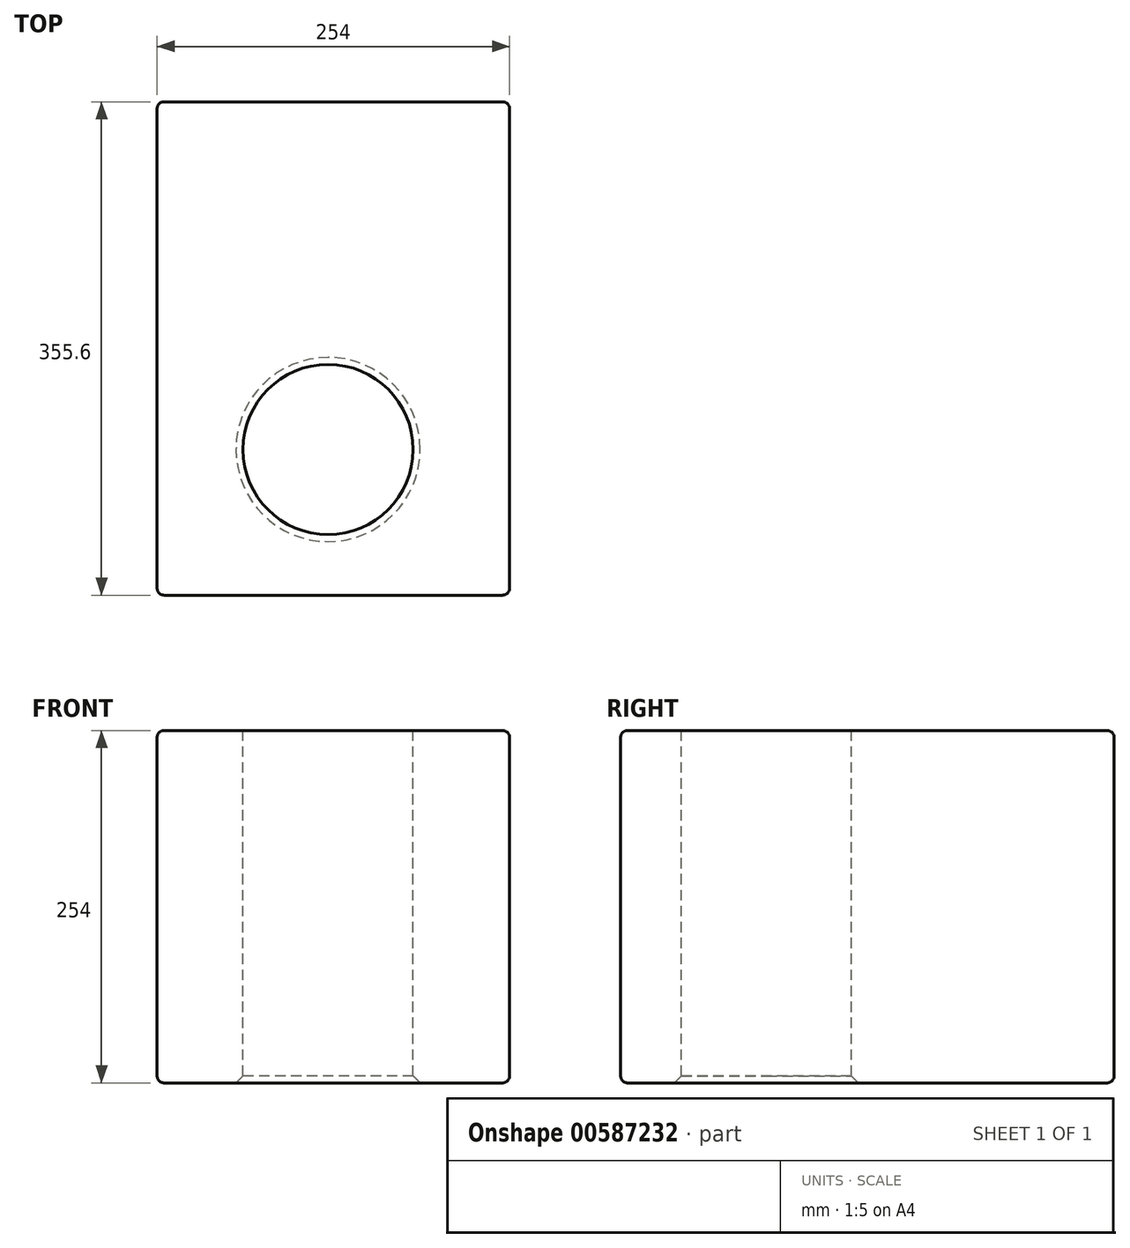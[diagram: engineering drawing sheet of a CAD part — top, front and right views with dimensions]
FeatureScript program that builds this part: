
annotation { "Feature Type Name" : "Feature", "Feature Type Description" : "" }
export const myFeature = defineFeature(function(context is Context, id is Id, definition is map)
    precondition{}
    {
        {
            var Q0;
            Q0=qCreatedBy(makeId("Top.planeOp"),FACE);
            var sketch = newSketch(context, id + "F0", { "sketchPlane" : qUnion([Q0])});
            skLineSegment(sketch, "E0.bottom", {"start": v(0, 0) * mm, "end": v(254, 0) * mm});
            skLineSegment(sketch, "E0.top", {"start": v(0, 355.6) * mm, "end": v(254, 355.6) * mm});
            skLineSegment(sketch, "E0.left", {"start": v(0, 0) * mm, "end": v(0, 355.6) * mm});
            skLineSegment(sketch, "E0.right", {"start": v(254, 0) * mm, "end": v(254, 355.6) * mm});
            skSolve(sketch);
        }
        {
            var Q0;
            Q0=makeQuery(id+"F0.imprint","IMPRINT",FACE,{"disambiguationData":[TD([[makeQuery(id+"F0.imprint","IMPRINT",EDGE,{"derivedFrom":sQuery(id+"F0.wireOp",EDGE,"E0.bottom")}),1.0]])]});
            extrude(context, id + "F1", {"entities" : qUnion([Q0]), "depth" : 254 * mm, "offsetDistance" : 25.4 * mm});
        }
        {
            var Q0;
            Q0=makeQuery(id+"F1.opExtrude","SWEPT_EDGE",EDGE,{"disambiguationData":[OSD([sQuery(id+"F0.wireOp",EDGE,"E0.bottom"),sQuery(id+"F0.wireOp",EDGE,"E0.right")])]});
            var Q1;
            Q1=makeQuery(id+"F1.opExtrude","SWEPT_EDGE",EDGE,{"disambiguationData":[OSD([sQuery(id+"F0.wireOp",EDGE,"E0.top"),sQuery(id+"F0.wireOp",EDGE,"E0.right")])]});
            var Q2;
            Q2=makeQuery(id+"F1.opExtrude","SWEPT_EDGE",EDGE,{"disambiguationData":[OSD([sQuery(id+"F0.wireOp",EDGE,"E0.bottom"),sQuery(id+"F0.wireOp",EDGE,"E0.left")])]});
            var Q3;
            Q3=makeQuery(id+"F1.opExtrude","CAP_EDGE",EDGE,{"disambiguationData":[OSD([sQuery(id+"F0.wireOp",EDGE,"E0.left")])],"isStart":true});
            var Q4;
            Q4=makeQuery(id+"F1.opExtrude","CAP_EDGE",EDGE,{"disambiguationData":[OSD([sQuery(id+"F0.wireOp",EDGE,"E0.top")])],"isStart":true});
            var Q5;
            Q5=makeQuery(id+"F1.opExtrude","CAP_EDGE",EDGE,{"disambiguationData":[OSD([sQuery(id+"F0.wireOp",EDGE,"E0.bottom")])],"isStart":true});
            var Q6;
            Q6=makeQuery(id+"F1.opExtrude","CAP_EDGE",EDGE,{"disambiguationData":[OSD([sQuery(id+"F0.wireOp",EDGE,"E0.right")])],"isStart":true});
            var Q7;
            Q7=makeQuery(id+"F1.opExtrude","SWEPT_EDGE",EDGE,{"disambiguationData":[OSD([sQuery(id+"F0.wireOp",EDGE,"E0.top"),sQuery(id+"F0.wireOp",EDGE,"E0.left")])]});
            var Q8;
            Q8=makeQuery(id+"F1.opExtrude","CAP_EDGE",EDGE,{"disambiguationData":[OSD([sQuery(id+"F0.wireOp",EDGE,"E0.left")])],"isStart":false});
            var Q9;
            Q9=makeQuery(id+"F1.opExtrude","CAP_EDGE",EDGE,{"disambiguationData":[OSD([sQuery(id+"F0.wireOp",EDGE,"E0.top")])],"isStart":false});
            var Q10;
            Q10=makeQuery(id+"F1.opExtrude","CAP_EDGE",EDGE,{"disambiguationData":[OSD([sQuery(id+"F0.wireOp",EDGE,"E0.right")])],"isStart":false});
            var Q11;
            Q11=makeQuery(id+"F1.opExtrude","CAP_EDGE",EDGE,{"disambiguationData":[OSD([sQuery(id+"F0.wireOp",EDGE,"E0.bottom")])],"isStart":false});
            fillet(context, id + "F2", {"entities" : qUnion([Q0, Q1, Q2, Q3, Q4, Q5, Q6, Q7, Q8, Q9, Q10, Q11]), "radius" : 5.08 * mm, "tangentPropagation" : true, "allowEdgeOverflow" : false});
        }
        {
            var Q0;
            Q0=makeQuery(id+"F1.opExtrude","CAP_FACE",FACE,{"disambiguationData":[OSD([sQuery(id+"F0.wireOp",EDGE,"E0.bottom"),sQuery(id+"F0.wireOp",EDGE,"E0.top"),sQuery(id+"F0.wireOp",EDGE,"E0.left"),sQuery(id+"F0.wireOp",EDGE,"E0.right")])],"isStart":false});
            var sketch = newSketch(context, id + "F3", { "sketchPlane" : qUnion([Q0])});
            skCircle(sketch, "E1", {"center": v(123.22, 105) * mm, "radius": 61.3 * mm});
            skSolve(sketch);
        }
        {
            var Q0;
            Q0=makeQuery(id+"F3.imprint","IMPRINT",FACE,{"disambiguationData":[TD([[makeQuery(id+"F3.imprint","IMPRINT",EDGE,{"derivedFrom":sQuery(id+"F3.wireOp",EDGE,"E1")}),1.0]])]});
            var Q1;
            Q1=sQuery(id+"F3.wireOp",EDGE,"E1");
            var Q2;
            Q2=makeQuery(id+"F1.opExtrude","CAP_FACE",FACE,{"disambiguationData":[OSD([sQuery(id+"F0.wireOp",EDGE,"E0.bottom"),sQuery(id+"F0.wireOp",EDGE,"E0.top"),sQuery(id+"F0.wireOp",EDGE,"E0.left"),sQuery(id+"F0.wireOp",EDGE,"E0.right")])],"isStart":false});
            extrude(context, id + "F4", {"entities" : qUnion([Q0]), "operationType" : NewBodyOperationType.REMOVE, "surfaceEntities" : qUnion([Q1]), "endBound" : BoundingType.THROUGH_ALL, "oppositeDirection" : true, "depth" : 254 * mm, "endBoundEntityFace" : qUnion([Q2]), "offsetDistance" : 25.4 * mm});
        }
        {
            var Q0;
            Q0=makeQuery(id+"F4.boolean.opBoolean","COPY",EDGE,{"derivedFrom":makeQuery(id+"F4.opExtrude","CAP_EDGE",EDGE,{"disambiguationData":[OSD([sQuery(id+"F3.wireOp",EDGE,"E1")])],"isStart":true})});
            var Q1;
            Q1=makeQuery(id+"F4.boolean.opBoolean","INTERSECT",EDGE,{"derivedFrom":[makeQuery(id+"F1.opExtrude","CAP_FACE",FACE,{"disambiguationData":[OSD([sQuery(id+"F0.wireOp",EDGE,"E0.bottom"),sQuery(id+"F0.wireOp",EDGE,"E0.top"),sQuery(id+"F0.wireOp",EDGE,"E0.left"),sQuery(id+"F0.wireOp",EDGE,"E0.right")])],"isStart":true}),makeQuery(id+"F4.opExtrude","SWEPT_FACE",FACE,{"disambiguationData":[OSD([sQuery(id+"F3.wireOp",EDGE,"E1")])]})]});
            chamfer(context, id + "F5", {"entities" : qUnion([Q0, Q1]), "width" : 5.08 * mm, "tangentPropagation" : true});
        }
    });
